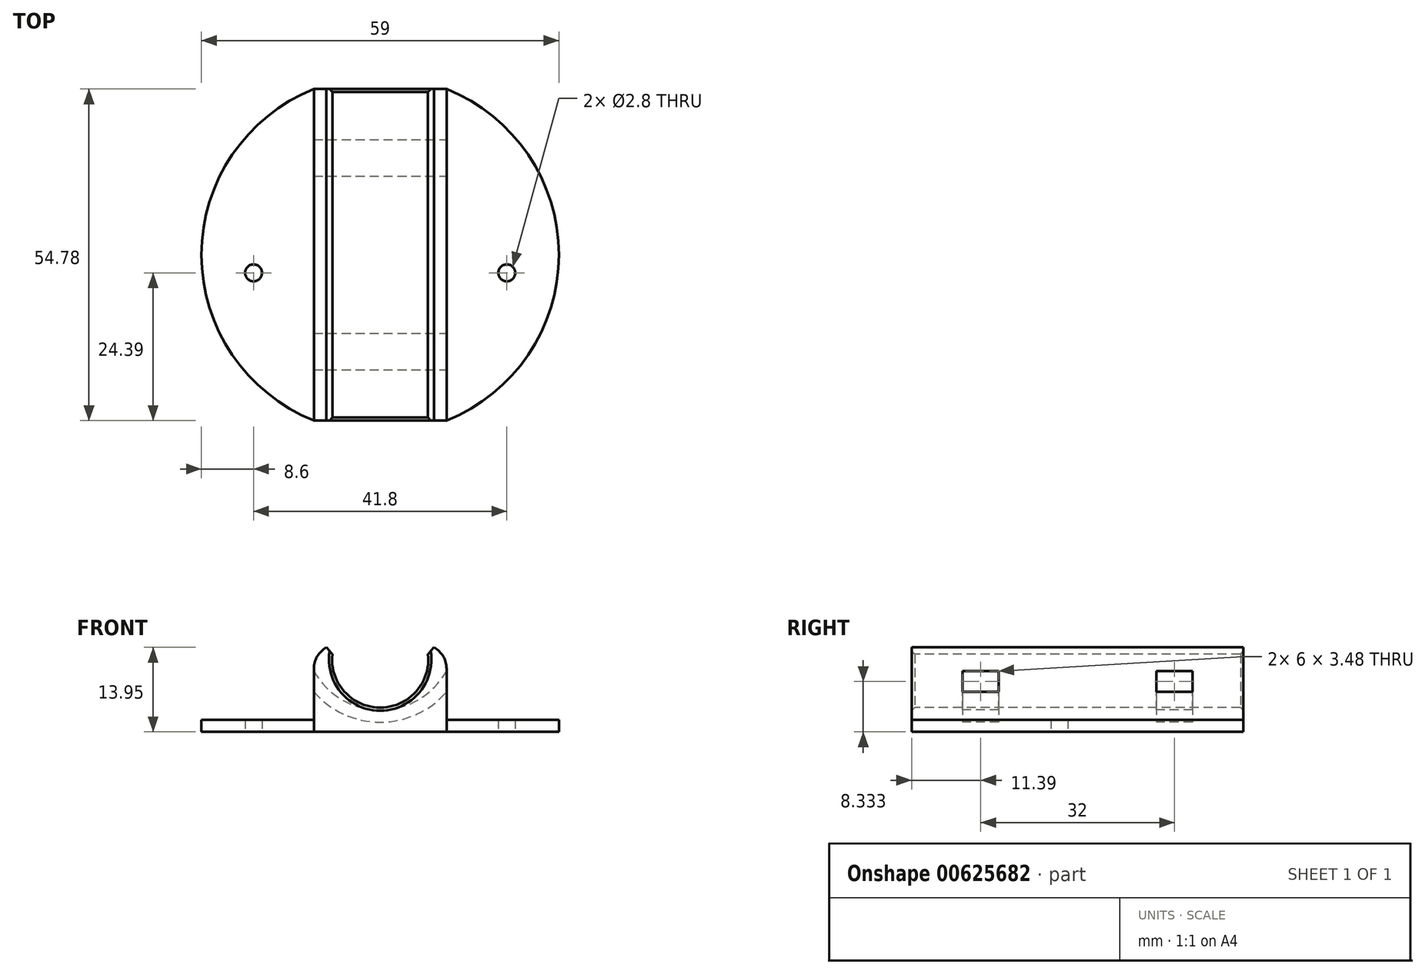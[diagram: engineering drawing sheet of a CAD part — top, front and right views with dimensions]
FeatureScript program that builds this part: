
annotation { "Feature Type Name" : "Feature", "Feature Type Description" : "" }
export const myFeature = defineFeature(function(context is Context, id is Id, definition is map)
    precondition{}
    {
        {
            var Q0;
            Q0=qCreatedBy(makeId("Top.planeOp"),FACE);
            var sketch = newSketch(context, id + "F0", { "sketchPlane" : qUnion([Q0])});
            skCircle(sketch, "E0", {"center": v(0, 0) * mm, "radius": 29.5 * mm});
            skLineSegment(sketch, "E1.bottom", {"start": v(7.95, -28.4) * mm, "end": v(-7.95, -28.4) * mm, "construction": true});
            skLineSegment(sketch, "E1.top", {"start": v(7.95, 28.4) * mm, "end": v(-7.95, 28.4) * mm, "construction": true});
            skLineSegment(sketch, "E1.left", {"start": v(7.95, -28.4) * mm, "end": v(7.95, 28.4) * mm, "construction": true});
            skLineSegment(sketch, "E1.right", {"start": v(-7.95, -28.4) * mm, "end": v(-7.95, 28.4) * mm, "construction": true});
            skLineSegment(sketch, "E2.bottom", {"start": v(-10.95, 27.4) * mm, "end": v(10.95, 27.4) * mm});
            skLineSegment(sketch, "E2.top", {"start": v(-10.95, -27.4) * mm, "end": v(10.95, -27.4) * mm});
            skLineSegment(sketch, "E2.left", {"start": v(-10.95, 27.4) * mm, "end": v(-10.95, -27.4) * mm});
            skLineSegment(sketch, "E2.right", {"start": v(10.95, 27.4) * mm, "end": v(10.95, -27.4) * mm});
            skCircle(sketch, "E3", {"center": v(20.9, -3) * mm, "radius": 1.4 * mm});
            skCircle(sketch, "E4.MirrorC", {"center": v(-20.9, -3) * mm, "radius": 1.4 * mm});
            skSolve(sketch);
        }
        {
            var Q0;
            Q0=qCreatedBy(makeId("Front.planeOp"),FACE);
            var sketch = newSketch(context, id + "F1", { "sketchPlane" : qUnion([Q0])});
            skCircle(sketch, "E5", {"center": v(0, 11.95) * mm, "radius": 7.95 * mm});
            skSolve(sketch);
        }
        {
            var Q0;
            Q0=makeQuery(id+"F0.imprint","IMPRINT",FACE,{"disambiguationData":[TD([[makeQuery(id+"F0.imprint","IMPRINT",EDGE,{"derivedFrom":sQuery(id+"F0.wireOp",EDGE,"E2.bottom")}),-1.0]])]});
            extrude(context, id + "F2", {"entities" : qUnion([Q0]), "depth" : (11.95 + 2) * mm, "offsetDistance" : 25 * mm});
        }
        {
            var Q0;
            {var subQ0=sQuery(id+"F0.wireOp",EDGE,"E2.right");Q0=makeQuery(id+"F0.imprint","IMPRINT",FACE,{"disambiguationData":[TD([[makeQuery(id+"F0.imprint","IMPRINT",EDGE,{"derivedFrom":subQ0}),1.0]])]});}
            var Q1;
            {var subQ0=sQuery(id+"F0.wireOp",EDGE,"E2.left");Q1=makeQuery(id+"F0.imprint","IMPRINT",FACE,{"disambiguationData":[TD([[makeQuery(id+"F0.imprint","IMPRINT",EDGE,{"derivedFrom":subQ0}),-1.0]])]});}
            extrude(context, id + "F3", {"entities" : qUnion([Q0, Q1]), "operationType" : NewBodyOperationType.ADD, "depth" : 2 * mm, "offsetDistance" : 25 * mm});
        }
        {
            var Q0;
            Q0=makeQuery(id+"F1.imprint","IMPRINT",FACE,{"disambiguationData":[TD([[makeQuery(id+"F1.imprint","IMPRINT",EDGE,{"derivedFrom":sQuery(id+"F1.wireOp",EDGE,"E5")}),1.0]])]});
            extrude(context, id + "F4", {"entities" : qUnion([Q0]), "operationType" : NewBodyOperationType.REMOVE, "endBound" : BoundingType.THROUGH_ALL, "oppositeDirection" : true, "depth" : 25 * mm, "offsetDistance" : 25 * mm, "hasSecondDirection" : true, "secondDirectionBound" : SecondDirectionBoundingType.THROUGH_ALL, "secondDirectionOppositeDirection" : false, "secondDirectionDepth" : 25 * mm});
        }
        {
            var Q0;
            Q0=qCreatedBy(makeId("Front.planeOp"),FACE);
            cPlane(context, id + "F5", {"entities" : qUnion([Q0]), "cplaneType" : CPlaneType.OFFSET, "offset" : 16 * mm, "width" : 150 * mm, "height" : 150 * mm});
        }
        {
            var Q0;
            Q0=qCreatedBy(makeId("Front.planeOp"),FACE);
            cPlane(context, id + "F6", {"entities" : qUnion([Q0]), "cplaneType" : CPlaneType.OFFSET, "offset" : 16 * mm, "oppositeDirection" : true, "width" : 150 * mm, "height" : 150 * mm});
        }
        {
            var Q0;
            Q0=qCreatedBy(id+"F5.planeOp",FACE);
            var sketch = newSketch(context, id + "F7", { "sketchPlane" : qUnion([Q0])});
            skCircle(sketch, "E6", {"center": v(0, 16.1) * mm, "radius": 12.5 * mm});
            skArc(sketch, "E7.0", {"start": v(7.7, 13.95) * mm, "mid": v(0, 4) * mm, "end": v(-7.7, 13.95) * mm});
            skCircle(sketch, "E8", {"center": v(0, 16.1) * mm, "radius": 14.5 * mm});
            skSolve(sketch);
        }
        {
            var Q0;
            Q0=qCreatedBy(id+"F6.planeOp",FACE);
            var sketch = newSketch(context, id + "F8", { "sketchPlane" : qUnion([Q0])});
            skCircle(sketch, "E9.0", {"center": v(0, 16.1) * mm, "radius": 12.5 * mm});
            skCircle(sketch, "E9.1", {"center": v(0, 16.1) * mm, "radius": 14.5 * mm});
            skSolve(sketch);
        }
        {
            var Q0;
            Q0=makeQuery(id+"F7.imprint","IMPRINT",FACE,{"disambiguationData":[TD([[makeQuery(id+"F7.imprint","IMPRINT",EDGE,{"derivedFrom":sQuery(id+"F7.wireOp",EDGE,"E6")}),-1.0]])]});
            var Q1;
            Q1=makeQuery(id+"F8.imprint","IMPRINT",FACE,{"disambiguationData":[TD([[makeQuery(id+"F8.imprint","IMPRINT",EDGE,{"derivedFrom":sQuery(id+"F8.wireOp",EDGE,"E9.0")}),-1.0]])]});
            extrude(context, id + "F9", {"entities" : qUnion([Q0, Q1]), "operationType" : NewBodyOperationType.REMOVE, "endBound" : BoundingType.SYMMETRIC, "oppositeDirection" : true, "depth" : 6 * mm, "offsetDistance" : 25 * mm});
        }
        {
            var Q0;
            Q0=makeQuery(id+"F4.boolean.opBoolean","INTERSECT",EDGE,{"disambiguationData":[OD(1.0)],"derivedFrom":[makeQuery(id+"F2.opExtrude","CAP_FACE",FACE,{"disambiguationData":[OSD([sQuery(id+"F0.wireOp",EDGE,"E2.bottom"),sQuery(id+"F0.wireOp",EDGE,"E2.top"),sQuery(id+"F0.wireOp",EDGE,"E2.left"),sQuery(id+"F0.wireOp",EDGE,"E2.right")])],"isStart":false}),makeQuery(id+"F4.opExtrude","SWEPT_FACE",FACE,{"disambiguationData":[OSD([sQuery(id+"F1.wireOp",EDGE,"E5")])]})]});
            var Q1;
            Q1=makeQuery(id+"F4.boolean.opBoolean","INTERSECT",EDGE,{"disambiguationData":[OD(0.0)],"derivedFrom":[makeQuery(id+"F2.opExtrude","CAP_FACE",FACE,{"disambiguationData":[OSD([sQuery(id+"F0.wireOp",EDGE,"E2.bottom"),sQuery(id+"F0.wireOp",EDGE,"E2.top"),sQuery(id+"F0.wireOp",EDGE,"E2.left"),sQuery(id+"F0.wireOp",EDGE,"E2.right")])],"isStart":false}),makeQuery(id+"F4.opExtrude","SWEPT_FACE",FACE,{"disambiguationData":[OSD([sQuery(id+"F1.wireOp",EDGE,"E5")])]})]});
            chamfer(context, id + "F10", {"entities" : qUnion([Q0, Q1]), "width" : 1 * mm, "tangentPropagation" : true});
        }
        {
            var Q0;
            Q0=makeQuery(id+"F2.opExtrude","CAP_EDGE",EDGE,{"disambiguationData":[OSD([sQuery(id+"F0.wireOp",EDGE,"E2.right")])],"isStart":false});
            var Q1;
            Q1=makeQuery(id+"F2.opExtrude","CAP_EDGE",EDGE,{"disambiguationData":[OSD([sQuery(id+"F0.wireOp",EDGE,"E2.left")])],"isStart":false});
            fillet(context, id + "F11", {"entities" : qUnion([Q0, Q1]), "radius" : 4 * mm, "tangentPropagation" : true, "allowEdgeOverflow" : false});
        }
        {
            var Q0;
            Q0=makeQuery(id+"F4.boolean.opBoolean","INTERSECT",EDGE,{"derivedFrom":[makeQuery(id+"F2.opExtrude","SWEPT_FACE",FACE,{"disambiguationData":[OSD([sQuery(id+"F0.wireOp",EDGE,"E2.bottom")])]}),makeQuery(id+"F4.opExtrude","SWEPT_FACE",FACE,{"disambiguationData":[OSD([sQuery(id+"F1.wireOp",EDGE,"E5")])]})]});
            var Q1;
            Q1=makeQuery(id+"F4.boolean.opBoolean","INTERSECT",EDGE,{"derivedFrom":[makeQuery(id+"F2.opExtrude","SWEPT_FACE",FACE,{"disambiguationData":[OSD([sQuery(id+"F0.wireOp",EDGE,"E2.top")])]}),makeQuery(id+"F4.opExtrude","SWEPT_FACE",FACE,{"disambiguationData":[OSD([sQuery(id+"F1.wireOp",EDGE,"E5")])]})]});
            chamfer(context, id + "F12", {"entities" : qUnion([Q0, Q1]), "width" : 0.5 * mm, "tangentPropagation" : true});
        }
    });
